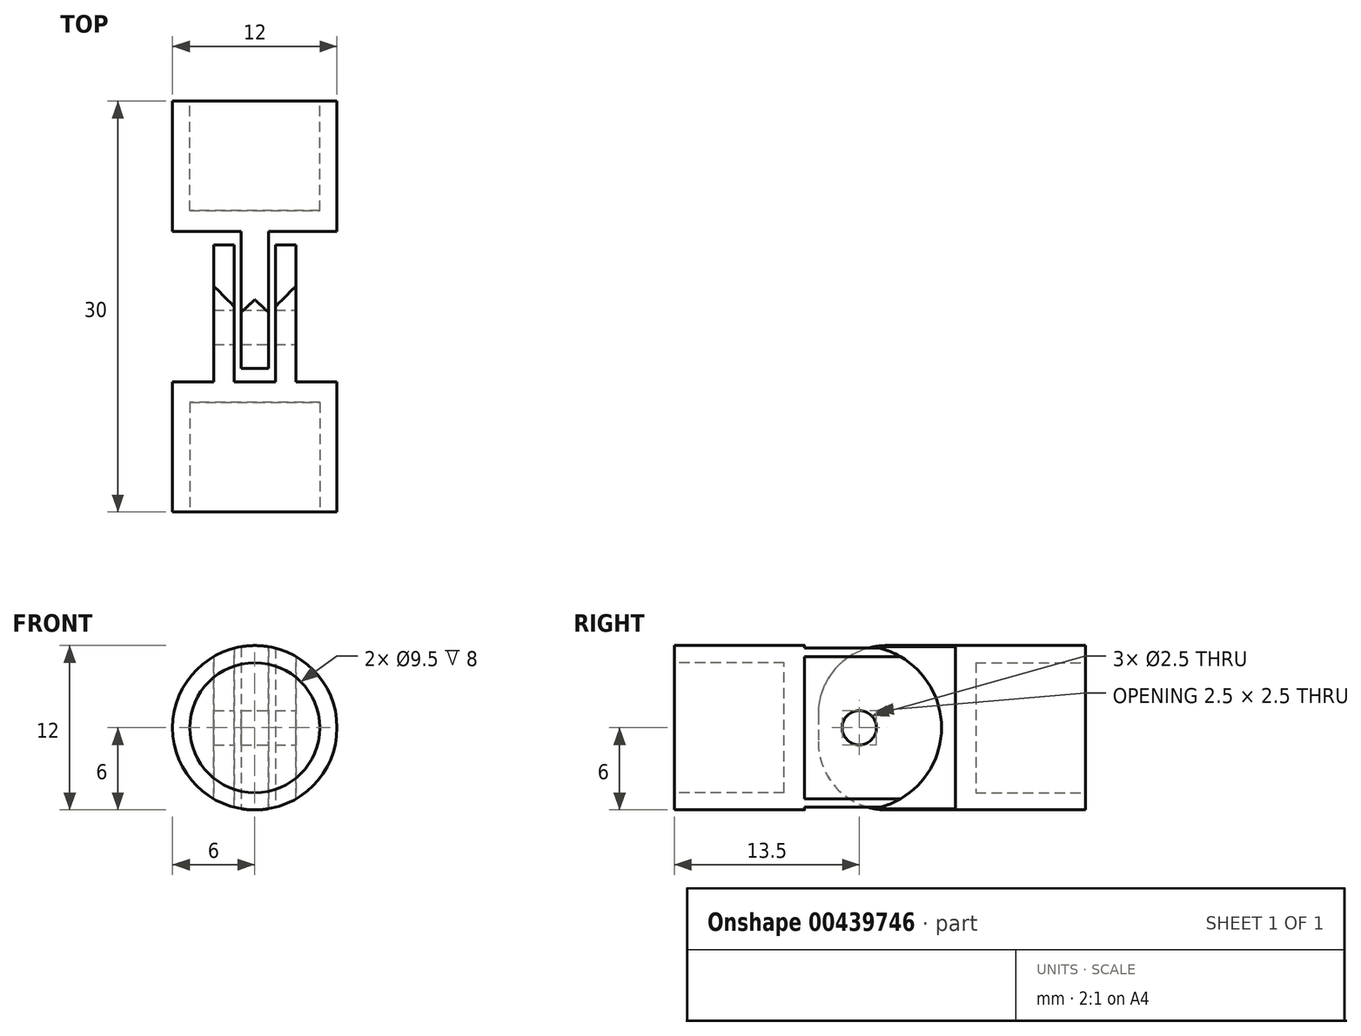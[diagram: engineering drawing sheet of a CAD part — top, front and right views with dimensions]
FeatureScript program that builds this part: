
annotation { "Feature Type Name" : "Feature", "Feature Type Description" : "" }
export const myFeature = defineFeature(function(context is Context, id is Id, definition is map)
    precondition{}
    {
        {
            var Q0;
            Q0=qCreatedBy(makeId("Top.planeOp"),FACE);
            var sketch = newSketch(context, id + "F0", { "sketchPlane" : qUnion([Q0])});
            skLineSegment(sketch, "E0.top", {"start": v(-6, -20.5) * mm, "end": v(6, -20.5) * mm});
            skLineSegment(sketch, "E0.left", {"start": v(-6, 9.5) * mm, "end": v(-6, 0) * mm});
            skLineSegment(sketch, "E0.right", {"start": v(6, 9.5) * mm, "end": v(6, 0) * mm});
            skLineSegment(sketch, "E1", {"start": v(-6, 0) * mm, "end": v(-1, 0) * mm});
            skLineSegment(sketch, "E2", {"start": v(-3, -1) * mm, "end": v(-1.5, -1) * mm});
            skLineSegment(sketch, "E3.trimOffspring", {"start": v(6, -11) * mm, "end": v(6, -20.5) * mm});
            skLineSegment(sketch, "E4.trimOffspring", {"start": v(-6, -11) * mm, "end": v(-6, -20.5) * mm});
            skLineSegment(sketch, "E5", {"start": v(-1, 0) * mm, "end": v(-1, -10) * mm});
            skLineSegment(sketch, "E6", {"start": v(-1, -10) * mm, "end": v(1, -10) * mm});
            skLineSegment(sketch, "E7", {"start": v(1, -10) * mm, "end": v(1, 0) * mm});
            skLineSegment(sketch, "E8", {"start": v(-1.5, -1) * mm, "end": v(-1.5, -11) * mm});
            skLineSegment(sketch, "E9", {"start": v(-1.5, -11) * mm, "end": v(1.5, -11) * mm});
            skLineSegment(sketch, "E10", {"start": v(1.5, -11) * mm, "end": v(1.5, -1) * mm});
            skLineSegment(sketch, "E11.trimOffspring", {"start": v(1.5, -1) * mm, "end": v(3, -1) * mm});
            skLineSegment(sketch, "E12", {"start": v(-3, -1) * mm, "end": v(-3, -11) * mm});
            skLineSegment(sketch, "E13", {"start": v(-3, -11) * mm, "end": v(-6, -11) * mm});
            skLineSegment(sketch, "E14", {"start": v(3, -1) * mm, "end": v(3, -11) * mm});
            skLineSegment(sketch, "E15", {"start": v(3, -11) * mm, "end": v(6, -11) * mm});
            skLineSegment(sketch, "E16.trimOffspring", {"start": v(1, 0) * mm, "end": v(6, 0) * mm});
            skLineSegment(sketch, "E17", {"start": v(-6, 9.5) * mm, "end": v(6, 9.5) * mm});
            skPoint(sketch, "E18.orphan", {"position": v(-6, 20) * mm});
            skSolve(sketch);
        }
        {
            var Q0;
            Q0=makeQuery(id+"F0.imprint","IMPRINT",FACE,{"disambiguationData":[TD([[makeQuery(id+"F0.imprint","IMPRINT",EDGE,{"derivedFrom":sQuery(id+"F0.wireOp",EDGE,"E0.left")}),1.0]])]});
            var Q1;
            Q1=makeQuery(id+"F0.imprint","IMPRINT",FACE,{"disambiguationData":[TD([[makeQuery(id+"F0.imprint","IMPRINT",EDGE,{"derivedFrom":sQuery(id+"F0.wireOp",EDGE,"E0.top")}),1.0]])]});
            extrude(context, id + "F1", {"entities" : qUnion([Q0, Q1]), "depth" : 12 * mm});
        }
        {
            var Q0;
            Q0=makeQuery(id+"F1.opExtrude","SWEPT_FACE",FACE,{"disambiguationData":[OSD([sQuery(id+"F0.wireOp",EDGE,"E0.top")])]});
            var sketch = newSketch(context, id + "F2", { "sketchPlane" : qUnion([Q0])});
            skCircle(sketch, "E19", {"center": v(0, 6) * mm, "radius": 6 * mm});
            skPoint(sketch, "E19.centerSnap0", {"position": v(0, 12) * mm});
            skLineSegment(sketch, "E20.bottom", {"start": v(-8.83, 13.69) * mm, "end": v(9.23, 13.69) * mm});
            skLineSegment(sketch, "E20.top", {"start": v(-8.83, -2.58) * mm, "end": v(9.23, -2.58) * mm});
            skLineSegment(sketch, "E20.left", {"start": v(-8.83, 13.69) * mm, "end": v(-8.83, -2.58) * mm});
            skLineSegment(sketch, "E20.right", {"start": v(9.23, 13.69) * mm, "end": v(9.23, -2.58) * mm});
            skSolve(sketch);
        }
        {
            var Q0;
            Q0=makeQuery(id+"F1.opExtrude","CAP_EDGE",EDGE,{"disambiguationData":[OSD([sQuery(id+"F0.wireOp",EDGE,"E11.trimOffspring")])],"isStart":false});
            var Q1;
            Q1=makeQuery(id+"F1.opExtrude","CAP_EDGE",EDGE,{"disambiguationData":[OSD([sQuery(id+"F0.wireOp",EDGE,"E11.trimOffspring")])],"isStart":true});
            var Q2;
            Q2=makeQuery(id+"F1.opExtrude","CAP_EDGE",EDGE,{"disambiguationData":[OSD([sQuery(id+"F0.wireOp",EDGE,"E2")])],"isStart":true});
            var Q3;
            Q3=makeQuery(id+"F1.opExtrude","CAP_EDGE",EDGE,{"disambiguationData":[OSD([sQuery(id+"F0.wireOp",EDGE,"E2")])],"isStart":false});
            fillet(context, id + "F3", {"entities" : qUnion([Q0, Q1, Q2, Q3]), "radius" : 6 * mm, "tangentPropagation" : true, "allowEdgeOverflow" : false});
        }
        {
            var Q0;
            Q0=makeQuery(id+"F1.opExtrude","CAP_EDGE",EDGE,{"disambiguationData":[OSD([sQuery(id+"F0.wireOp",EDGE,"E6")])],"isStart":false});
            var Q1;
            Q1=makeQuery(id+"F1.opExtrude","CAP_EDGE",EDGE,{"disambiguationData":[OSD([sQuery(id+"F0.wireOp",EDGE,"E6")])],"isStart":true});
            fillet(context, id + "F4", {"entities" : qUnion([Q0, Q1]), "radius" : 5 * mm, "tangentPropagation" : true, "allowEdgeOverflow" : false});
        }
        {
            var Q0;
            Q0 = qSketchRegion(id + "F2", true);
            extrude(context, id + "F5", {"entities" : qUnion([Q0]), "operationType" : NewBodyOperationType.REMOVE, "oppositeDirection" : true, "depth" : 35.7 * mm});
        }
        {
            var Q0;
            Q0=makeQuery(id+"F1.opExtrude","SWEPT_FACE",FACE,{"disambiguationData":[OSD([sQuery(id+"F0.wireOp",EDGE,"E14")])]});
            var sketch = newSketch(context, id + "F6", { "sketchPlane" : qUnion([Q0])});
            skCircle(sketch, "E21", {"center": v(-7, 6) * mm, "radius": 1.25 * mm});
            skSolve(sketch);
        }
        {
            var Q0;
            Q0=makeQuery(id+"F6.imprint","IMPRINT",FACE,{"disambiguationData":[TD([[makeQuery(id+"F6.imprint","IMPRINT",EDGE,{"derivedFrom":sQuery(id+"F6.wireOp",EDGE,"E21")}),1.0]])]});
            extrude(context, id + "F7", {"entities" : qUnion([Q0]), "operationType" : NewBodyOperationType.REMOVE, "oppositeDirection" : true, "depth" : 25 * mm});
        }
        {
            var Q0;
            Q0=makeQuery(id+"F1.opExtrude","SWEPT_FACE",FACE,{"disambiguationData":[OSD([sQuery(id+"F0.wireOp",EDGE,"E0.top")])]});
            var sketch = newSketch(context, id + "F8", { "sketchPlane" : qUnion([Q0])});
            skCircle(sketch, "E22", {"center": v(0, 6) * mm, "radius": 4.75 * mm});
            skSolve(sketch);
        }
        {
            var Q0;
            Q0=makeQuery(id+"F8.imprint","IMPRINT",FACE,{"disambiguationData":[TD([[makeQuery(id+"F8.imprint","IMPRINT",EDGE,{"derivedFrom":sQuery(id+"F8.wireOp",EDGE,"E22")}),1.0]])]});
            extrude(context, id + "F9", {"entities" : qUnion([Q0]), "operationType" : NewBodyOperationType.REMOVE, "oppositeDirection" : true, "depth" : 8 * mm});
        }
        {
            var Q0;
            Q0=makeQuery(id+"F1.opExtrude","SWEPT_FACE",FACE,{"disambiguationData":[OSD([sQuery(id+"F0.wireOp",EDGE,"E17")])]});
            var sketch = newSketch(context, id + "F10", { "sketchPlane" : qUnion([Q0])});
            skCircle(sketch, "E23", {"center": v(0, 6) * mm, "radius": 4.75 * mm});
            skSolve(sketch);
        }
        {
            var Q0;
            Q0=makeQuery(id+"F10.imprint","IMPRINT",FACE,{"disambiguationData":[TD([[makeQuery(id+"F10.imprint","IMPRINT",EDGE,{"derivedFrom":sQuery(id+"F10.wireOp",EDGE,"E23")}),1.0]])]});
            extrude(context, id + "F11", {"entities" : qUnion([Q0]), "operationType" : NewBodyOperationType.REMOVE, "oppositeDirection" : true, "depth" : 8 * mm});
        }
    });
